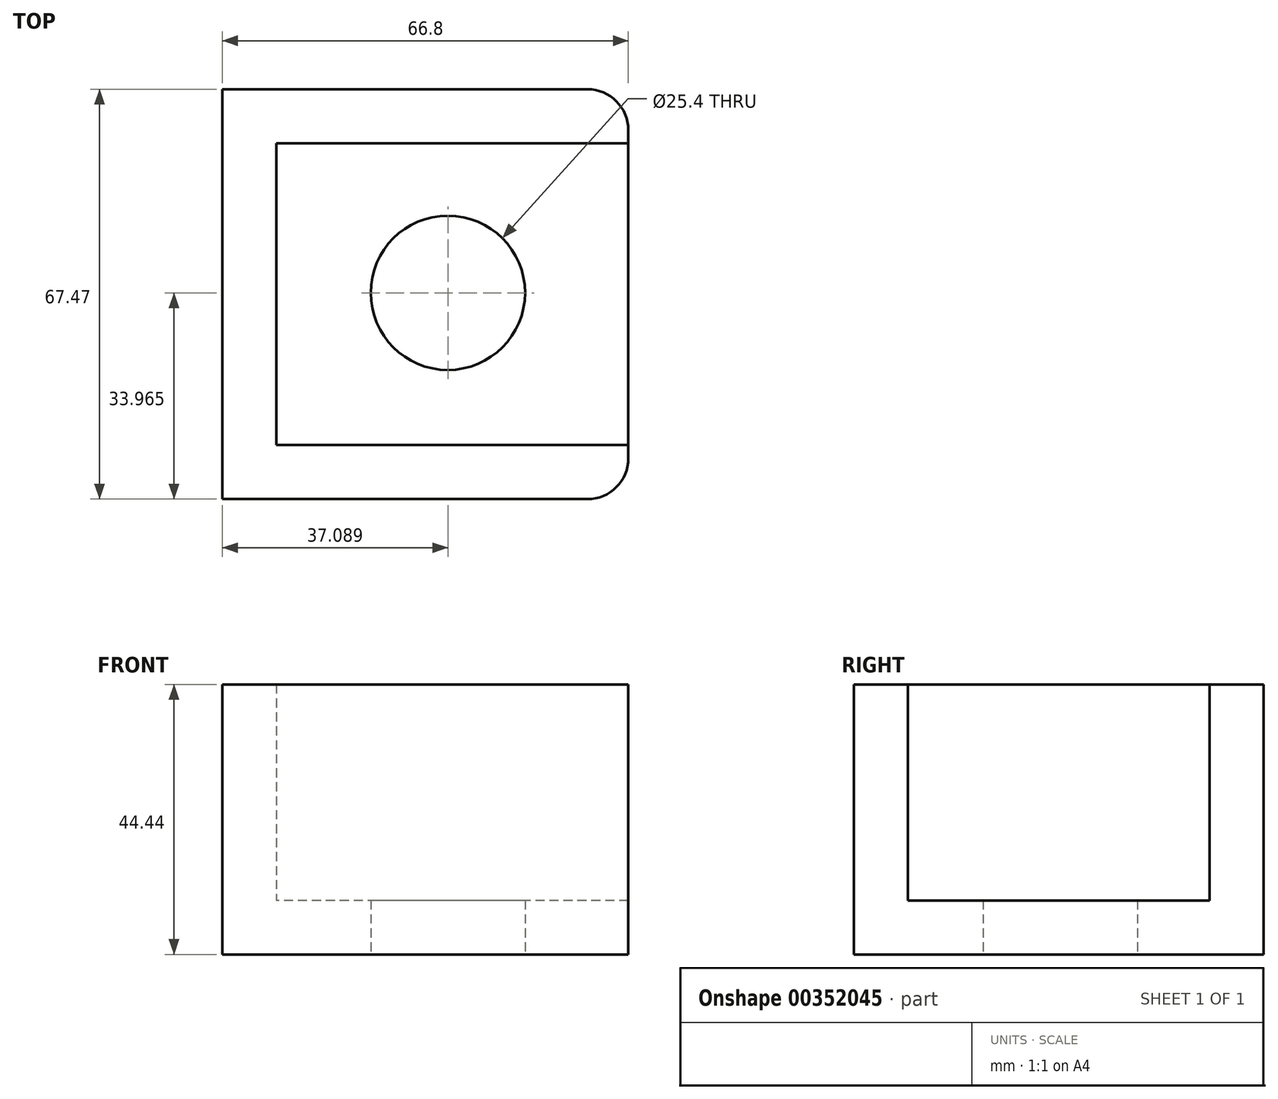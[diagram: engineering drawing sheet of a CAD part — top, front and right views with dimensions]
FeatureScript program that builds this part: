
annotation { "Feature Type Name" : "Feature", "Feature Type Description" : "" }
export const myFeature = defineFeature(function(context is Context, id is Id, definition is map)
    precondition{}
    {
        {
            var Q0;
            Q0=qCreatedBy(makeId("Right.planeOp"),FACE);
            var sketch = newSketch(context, id + "F0", { "sketchPlane" : qUnion([Q0])});
            skLineSegment(sketch, "E0.bottom", {"start": v(-67.47, 44.44) * mm, "end": v(0, 44.44) * mm});
            skLineSegment(sketch, "E0.top", {"start": v(-67.47, 0) * mm, "end": v(0, 0) * mm});
            skLineSegment(sketch, "E0.left", {"start": v(-67.47, 44.44) * mm, "end": v(-67.47, 0) * mm});
            skLineSegment(sketch, "E0.right", {"start": v(0, 44.44) * mm, "end": v(0, 0) * mm});
            skSolve(sketch);
        }
        {
            var Q0;
            Q0=makeQuery(id+"F0.imprint","IMPRINT",FACE,{"disambiguationData":[TD([[makeQuery(id+"F0.imprint","IMPRINT",EDGE,{"derivedFrom":sQuery(id+"F0.wireOp",EDGE,"E0.bottom")}),-1.0]])]});
            extrude(context, id + "F1", {"entities" : qUnion([Q0]), "depth" : 66.8 * mm});
        }
        {
            var Q0;
            Q0=makeQuery(id+"F1.opExtrude","CAP_EDGE",EDGE,{"disambiguationData":[OSD([sQuery(id+"F0.wireOp",EDGE,"E0.right")])],"isStart":false});
            var Q1;
            Q1=makeQuery(id+"F1.opExtrude","CAP_EDGE",EDGE,{"disambiguationData":[OSD([sQuery(id+"F0.wireOp",EDGE,"E0.left")])],"isStart":false});
            fillet(context, id + "F2", {"entities" : qUnion([Q0, Q1]), "radius" : 6.75 * mm, "tangentPropagation" : true, "allowEdgeOverflow" : false});
        }
        {
            var Q0;
            Q0=makeQuery(id+"F1.opExtrude","SWEPT_FACE",FACE,{"disambiguationData":[OSD([sQuery(id+"F0.wireOp",EDGE,"E0.bottom")])]});
            var Q1;
            Q1=makeQuery(id+"F1.opExtrude","CAP_FACE",FACE,{"disambiguationData":[OSD([sQuery(id+"F0.wireOp",EDGE,"E0.bottom"),sQuery(id+"F0.wireOp",EDGE,"E0.top"),sQuery(id+"F0.wireOp",EDGE,"E0.left"),sQuery(id+"F0.wireOp",EDGE,"E0.right")])],"isStart":false});
            shell(context, id + "F3", {"entities" : qUnion([Q0, Q1]), "thickness" : 8.9 * mm});
        }
        {
            var Q0;
            Q0=qCreatedBy(makeId("Top.planeOp"),FACE);
            var sketch = newSketch(context, id + "F4", { "sketchPlane" : qUnion([Q0])});
            skCircle(sketch, "E1", {"center": v(37.09, -33.5) * mm, "radius": 8.45 * mm});
            skSolve(sketch);
        }
        {
            var Q0;
            Q0=sQuery(id+"F4.wireOp",VERTEX,"E1.center");
            var Q1;
            Q1=makeQuery(id+"F1.opExtrude","SWEPT_BODY",BODY,{"disambiguationData":[OSD([sQuery(id+"F0.wireOp",EDGE,"E0.bottom"),sQuery(id+"F0.wireOp",EDGE,"E0.top"),sQuery(id+"F0.wireOp",EDGE,"E0.left"),sQuery(id+"F0.wireOp",EDGE,"E0.right")])]});
            hole(context, id + "F5", {"style" : HoleStyle.C_BORE, "endStyle" : HoleEndStyle.THROUGH, "oppositeDirection" : true, "holeDiameter" : 19.05 * mm, "cBoreDiameter" : 25.4 * mm, "cBoreDepth" : 12.7 * mm, "isTappedThrough" : true, "tappedDepth" : 12.7 * mm, "tapClearance" : 3, "startFromSketch" : true, "locations" : qUnion([Q0]), "scope" : qUnion([Q1])});
        }
    });
